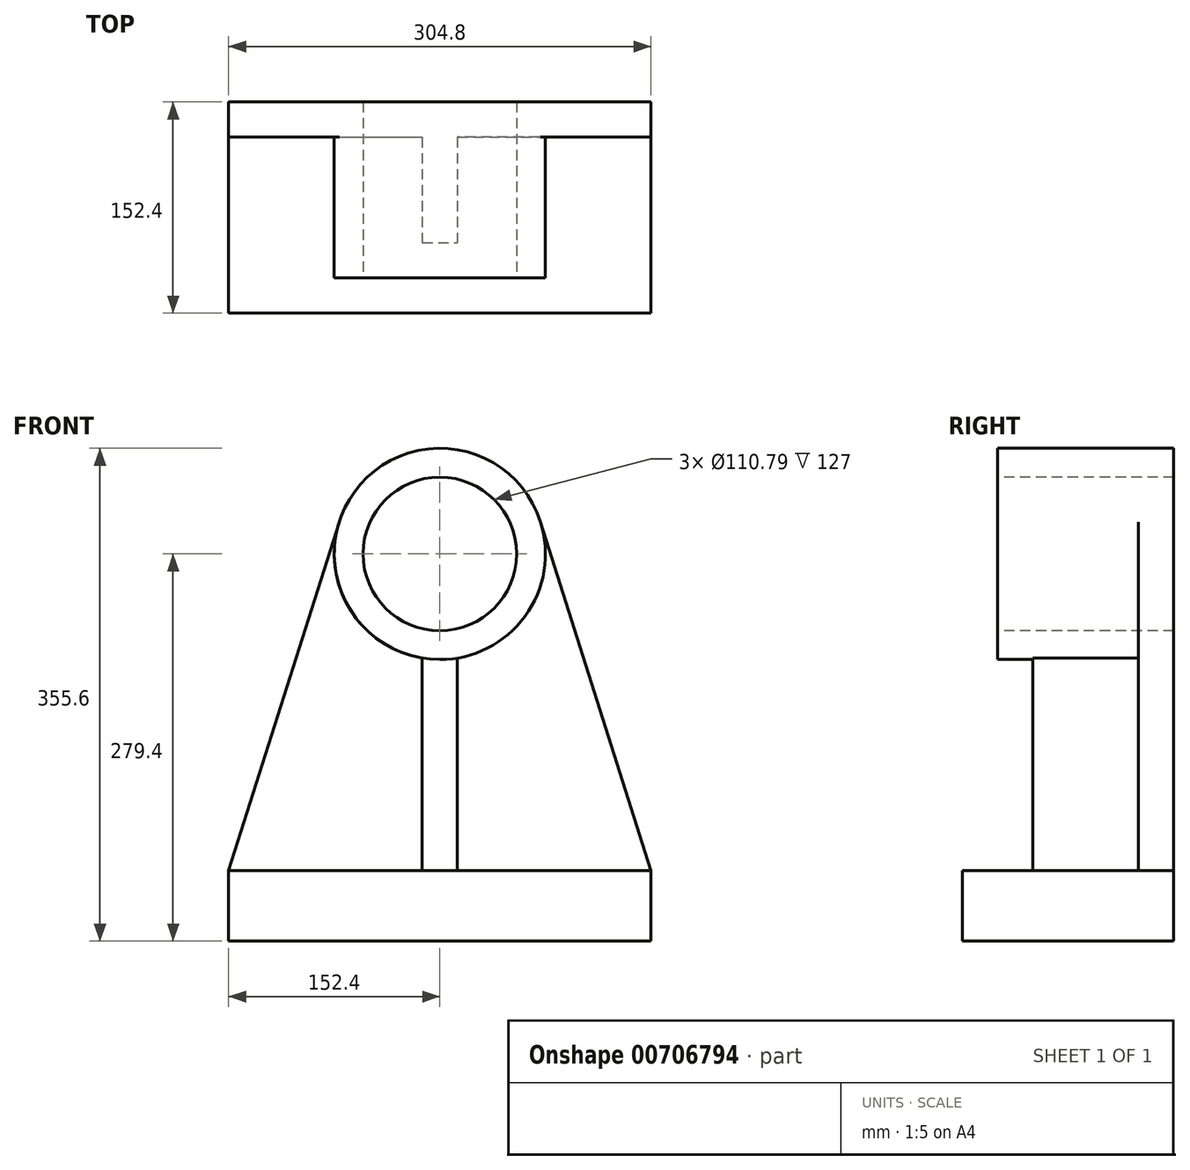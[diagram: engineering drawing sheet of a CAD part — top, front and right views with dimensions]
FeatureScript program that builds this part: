
annotation { "Feature Type Name" : "Feature", "Feature Type Description" : "" }
export const myFeature = defineFeature(function(context is Context, id is Id, definition is map)
    precondition{}
    {
        {
            var Q0;
            Q0=qCreatedBy(makeId("Front.planeOp"),FACE);
            var sketch = newSketch(context, id + "F0", { "sketchPlane" : qUnion([Q0])});
            skLineSegment(sketch, "E0.bottom", {"start": v(152.4, -25.4) * mm, "end": v(-152.4, -25.4) * mm});
            skLineSegment(sketch, "E0.left", {"start": v(152.4, -25.4) * mm, "end": v(152.4, 25.4) * mm});
            skLineSegment(sketch, "E0.right", {"start": v(-152.4, -25.4) * mm, "end": v(-152.4, 25.4) * mm});
            skPoint(sketch, "E0.middle", {"position": v(0, 0) * mm});
            skArc(sketch, "E1", {"start": v(72.64, 277.03) * mm, "mid": v(0, 330.2) * mm, "end": v(-72.64, 277.03) * mm});
            skLineSegment(sketch, "E2", {"start": v(-152.4, 25.4) * mm, "end": v(-72.64, 277.03) * mm});
            skLineSegment(sketch, "E3", {"start": v(152.4, 25.4) * mm, "end": v(72.64, 277.03) * mm});
            skSolve(sketch);
        }
        {
            var Q0;
            Q0 = qSketchRegion(id + "F0", true);
            extrude(context, id + "F1", {"entities" : qUnion([Q0]), "depth" : 152.4 * mm, "offsetDistance" : 25.4 * mm});
        }
        {
            var Q0;
            Q0=makeQuery(id+"F1.opExtrude","CAP_FACE",FACE,{"disambiguationData":[OSD([sQuery(id+"F0.wireOp",EDGE,"E0.bottom"),sQuery(id+"F0.wireOp",EDGE,"E0.left"),sQuery(id+"F0.wireOp",EDGE,"E0.right"),sQuery(id+"F0.wireOp",EDGE,"E1"),sQuery(id+"F0.wireOp",EDGE,"E2"),sQuery(id+"F0.wireOp",EDGE,"E3")])],"isStart":false});
            var sketch = newSketch(context, id + "F2", { "sketchPlane" : qUnion([Q0])});
            skArc(sketch, "E4", {"start": v(-72.64, 277.03) * mm, "mid": v(-65.03, 214.29) * mm, "end": v(-12.7, 178.87) * mm});
            skLineSegment(sketch, "E5", {"start": v(-152.4, 25.4) * mm, "end": v(-12.7, 25.4) * mm});
            skLineSegment(sketch, "E6", {"start": v(-152.4, 25.4) * mm, "end": v(-72.64, 277.03) * mm});
            skLineSegment(sketch, "E7", {"start": v(-12.7, 25.4) * mm, "end": v(-12.7, 178.87) * mm});
            skLineSegment(sketch, "E8", {"start": v(152.4, 25.4) * mm, "end": v(12.7, 25.4) * mm});
            skLineSegment(sketch, "E9", {"start": v(12.7, 25.4) * mm, "end": v(12.7, 178.87) * mm});
            skLineSegment(sketch, "E10", {"start": v(152.4, 25.4) * mm, "end": v(72.64, 277.03) * mm});
            skArc(sketch, "E11.trimOffspring", {"start": v(12.7, 178.87) * mm, "mid": v(65.03, 214.29) * mm, "end": v(72.64, 277.03) * mm});
            skSolve(sketch);
        }
        {
            var Q0;
            Q0 = qSketchRegion(id + "F2", true);
            extrude(context, id + "F3", {"entities" : qUnion([Q0]), "operationType" : NewBodyOperationType.REMOVE, "oppositeDirection" : true, "depth" : 127 * mm, "offsetDistance" : 25.4 * mm});
        }
        {
            var Q0;
            Q0=makeQuery(id+"F1.opExtrude","CAP_FACE",FACE,{"disambiguationData":[OSD([sQuery(id+"F0.wireOp",EDGE,"E0.bottom"),sQuery(id+"F0.wireOp",EDGE,"E0.left"),sQuery(id+"F0.wireOp",EDGE,"E0.right"),sQuery(id+"F0.wireOp",EDGE,"E1"),sQuery(id+"F0.wireOp",EDGE,"E2"),sQuery(id+"F0.wireOp",EDGE,"E3")])],"isStart":false});
            var sketch = newSketch(context, id + "F4", { "sketchPlane" : qUnion([Q0])});
            skCircle(sketch, "E12", {"center": v(0, 254) * mm, "radius": 55.4 * mm});
            skSolve(sketch);
        }
        {
            var Q0;
            Q0 = qSketchRegion(id + "F4", true);
            extrude(context, id + "F5", {"entities" : qUnion([Q0]), "operationType" : NewBodyOperationType.REMOVE, "oppositeDirection" : true, "depth" : 152.4 * mm, "offsetDistance" : 25.4 * mm});
        }
        {
            var Q0;
            Q0=makeQuery(id+"F1.opExtrude","CAP_FACE",FACE,{"disambiguationData":[OSD([sQuery(id+"F0.wireOp",EDGE,"E0.bottom"),sQuery(id+"F0.wireOp",EDGE,"E0.left"),sQuery(id+"F0.wireOp",EDGE,"E0.right"),sQuery(id+"F0.wireOp",EDGE,"E1"),sQuery(id+"F0.wireOp",EDGE,"E2"),sQuery(id+"F0.wireOp",EDGE,"E3")])],"isStart":false});
            var sketch = newSketch(context, id + "F6", { "sketchPlane" : qUnion([Q0])});
            skLineSegment(sketch, "E13.bottom", {"start": v(-152.4, 25.4) * mm, "end": v(152.4, 25.4) * mm});
            skLineSegment(sketch, "E13.top", {"start": v(-152.4, 25.4) * mm, "end": v(152.4, 25.4) * mm});
            skLineSegment(sketch, "E13.left", {"start": v(-152.4, 25.4) * mm, "end": v(-152.4, 25.4) * mm});
            skLineSegment(sketch, "E13.right", {"start": v(152.4, 25.4) * mm, "end": v(152.4, 25.4) * mm});
            skLineSegment(sketch, "E14.top", {"start": v(-152.4, 341.26) * mm, "end": v(152.4, 341.26) * mm});
            skLineSegment(sketch, "E14.left", {"start": v(-152.4, 25.4) * mm, "end": v(-152.4, 341.26) * mm});
            skLineSegment(sketch, "E14.right", {"start": v(152.4, 25.4) * mm, "end": v(152.4, 341.26) * mm});
            skSolve(sketch);
        }
        {
            var Q0;
            Q0 = qSketchRegion(id + "F6", true);
            extrude(context, id + "F7", {"entities" : qUnion([Q0]), "operationType" : NewBodyOperationType.REMOVE, "oppositeDirection" : true, "depth" : 25.4 * mm, "offsetDistance" : 25.4 * mm});
        }
        {
            var Q0;
            Q0=makeQuery(id+"F7.boolean.opBoolean","COPY",FACE,{"derivedFrom":makeQuery(id+"F7.opExtrude","CAP_FACE",FACE,{"disambiguationData":[OSD([sQuery(id+"F6.wireOp",EDGE,"E13.bottom"),sQuery(id+"F6.wireOp",EDGE,"E14.top"),sQuery(id+"F6.wireOp",EDGE,"E14.left"),sQuery(id+"F6.wireOp",EDGE,"E14.right")])],"isStart":false})});
            var sketch = newSketch(context, id + "F8", { "sketchPlane" : qUnion([Q0])});
            skArc(sketch, "E15", {"start": v(-12.7, 178.87) * mm, "mid": v(0, 177.8) * mm, "end": v(12.7, 178.87) * mm});
            skLineSegment(sketch, "E16", {"start": v(-12.7, 178.87) * mm, "end": v(-12.7, 25.4) * mm});
            skLineSegment(sketch, "E17", {"start": v(-12.7, 25.4) * mm, "end": v(12.7, 25.4) * mm});
            skLineSegment(sketch, "E18", {"start": v(12.7, 25.4) * mm, "end": v(12.7, 178.87) * mm});
            skSolve(sketch);
        }
        {
            var Q0;
            Q0 = qSketchRegion(id + "F8", true);
            extrude(context, id + "F9", {"entities" : qUnion([Q0]), "operationType" : NewBodyOperationType.REMOVE, "oppositeDirection" : true, "depth" : 25.4 * mm, "offsetDistance" : 25.4 * mm});
        }
    });
